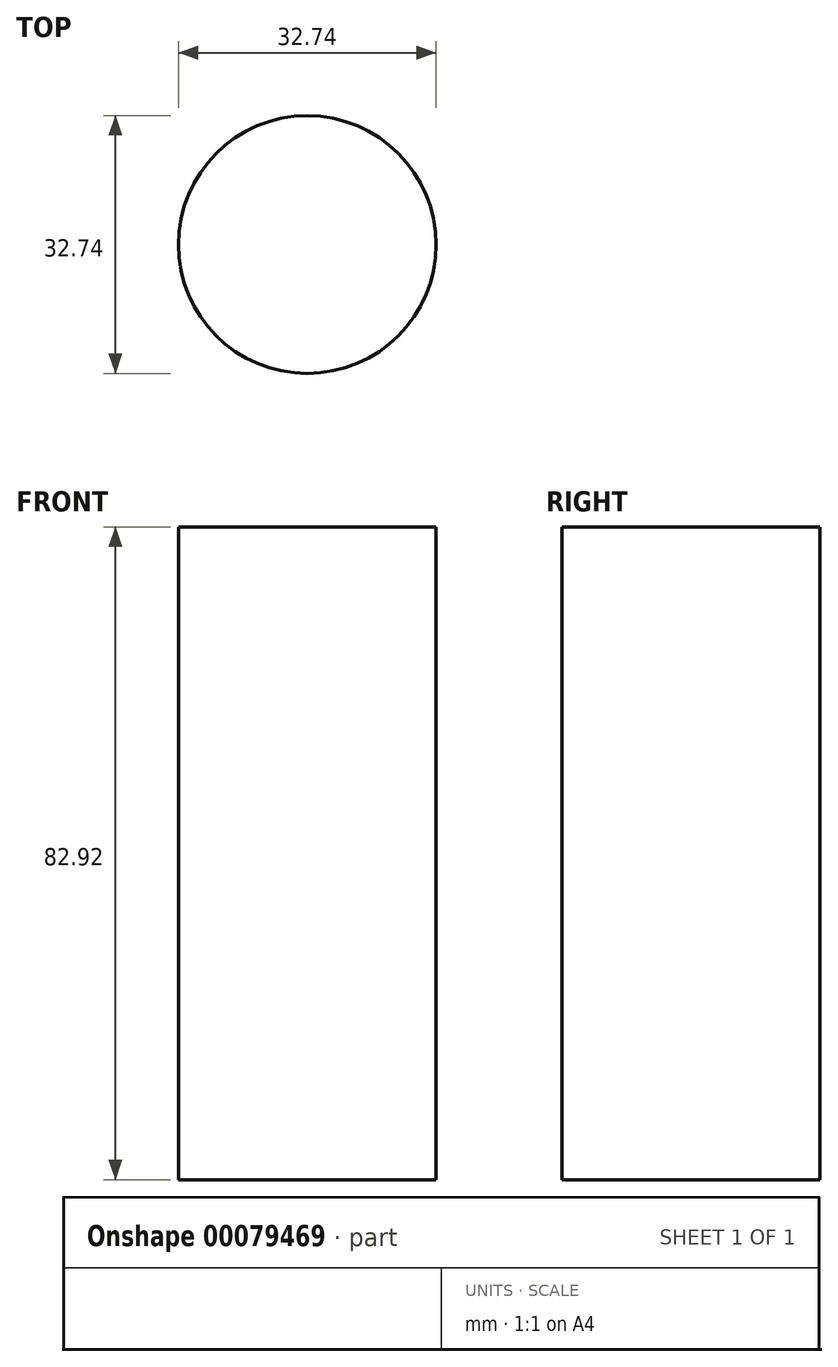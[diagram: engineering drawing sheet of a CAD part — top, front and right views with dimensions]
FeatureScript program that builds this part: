
annotation { "Feature Type Name" : "Feature", "Feature Type Description" : "" }
export const myFeature = defineFeature(function(context is Context, id is Id, definition is map)
    precondition{}
    {
        {
            var Q0;
            Q0=qCreatedBy(makeId("Front.planeOp"),FACE);
            var sketch = newSketch(context, id + "F0", { "sketchPlane" : qUnion([Q0])});
            skLineSegment(sketch, "E0", {"start": v(2.37, 60.65) * mm, "end": v(-15.05, 60.65) * mm});
            skLineSegment(sketch, "E1", {"start": v(-15.05, 60.65) * mm, "end": v(-15.05, 42.33) * mm});
            skLineSegment(sketch, "E2", {"start": v(-15.05, 42.33) * mm, "end": v(-31.76, 42.33) * mm});
            skLineSegment(sketch, "E3", {"start": v(-31.76, 42.33) * mm, "end": v(-31.76, -22.7) * mm});
            skLineSegment(sketch, "E4", {"start": v(-31.76, -22.7) * mm, "end": v(-17.57, -22.7) * mm});
            skLineSegment(sketch, "E5", {"start": v(-17.57, -22.7) * mm, "end": v(-17.57, -36) * mm});
            skLineSegment(sketch, "E6", {"start": v(-17.57, -36) * mm, "end": v(5.06, -36) * mm});
            skLineSegment(sketch, "E7", {"start": v(5.06, -36) * mm, "end": v(5.06, 60.65) * mm});
            skLineSegment(sketch, "E8", {"start": v(5.06, 60.65) * mm, "end": v(2.37, 60.65) * mm});
            skSolve(sketch);
        }
        {
            var Q0;
            Q0=sQuery(id+"F0.wireOp",EDGE,"E3");
            var Q1;
            Q1=sQuery(id+"F0.wireOp",EDGE,"E2");
            var Q2;
            Q2=sQuery(id+"F0.wireOp",EDGE,"E1");
            var Q3;
            Q3=sQuery(id+"F0.wireOp",EDGE,"E0");
            var Q4;
            Q4=sQuery(id+"F0.wireOp",EDGE,"E8");
            var Q5;
            Q5=sQuery(id+"F0.wireOp",EDGE,"E4");
            var Q6;
            Q6=sQuery(id+"F0.wireOp",EDGE,"E5");
            var Q7;
            Q7=sQuery(id+"F0.wireOp",EDGE,"E6");
            var Q8;
            Q8=sQuery(id+"F0.wireOp",EDGE,"E7");
            revolve(context, id + "F1", {"bodyType" : ToolBodyType.SURFACE, "surfaceEntities" : qUnion([Q0, Q1, Q2, Q3, Q4, Q5, Q6, Q7]), "axis" : qUnion([Q8]), "revolveType" : RevolveType.FULL});
        }
        {
            var Q0;
            Q0=makeQuery(id+"F1.opRevolve","SWEPT_EDGE",EDGE,{"disambiguationData":[OSD([sQuery(id+"F0.wireOp",VERTEX,"E2.end")])]});
            var Q1;
            Q1=makeQuery(id+"F1.opRevolve","SWEPT_EDGE",EDGE,{"disambiguationData":[OSD([sQuery(id+"F0.wireOp",VERTEX,"E4.start")])]});
            fillet(context, id + "F2", {"entities" : qUnion([Q0, Q1]), "radius" : 5.08 * mm, "tangentPropagation" : true, "allowEdgeOverflow" : false});
        }
        {
            var Q0;
            Q0=makeQuery(id+"F1.opRevolve","SWEPT_FACE",FACE,{"disambiguationData":[OSD([sQuery(id+"F0.wireOp",EDGE,"E6")])]});
            var sketch = newSketch(context, id + "F3", { "sketchPlane" : qUnion([Q0])});
            skCircle(sketch, "E9", {"center": v(5.06, 0) * mm, "radius": 16.37 * mm});
            skSolve(sketch);
        }
        {
            var Q0;
            Q0=makeQuery(id+"F3.imprint","IMPRINT",FACE,{"disambiguationData":[TD([[makeQuery(id+"F3.imprint","IMPRINT",EDGE,{"derivedFrom":sQuery(id+"F3.wireOp",EDGE,"E9")}),1.0]])]});
            extrude(context, id + "F4", {"entities" : qUnion([Q0]), "oppositeDirection" : true, "depth" : 82.92 * mm});
        }
    });
